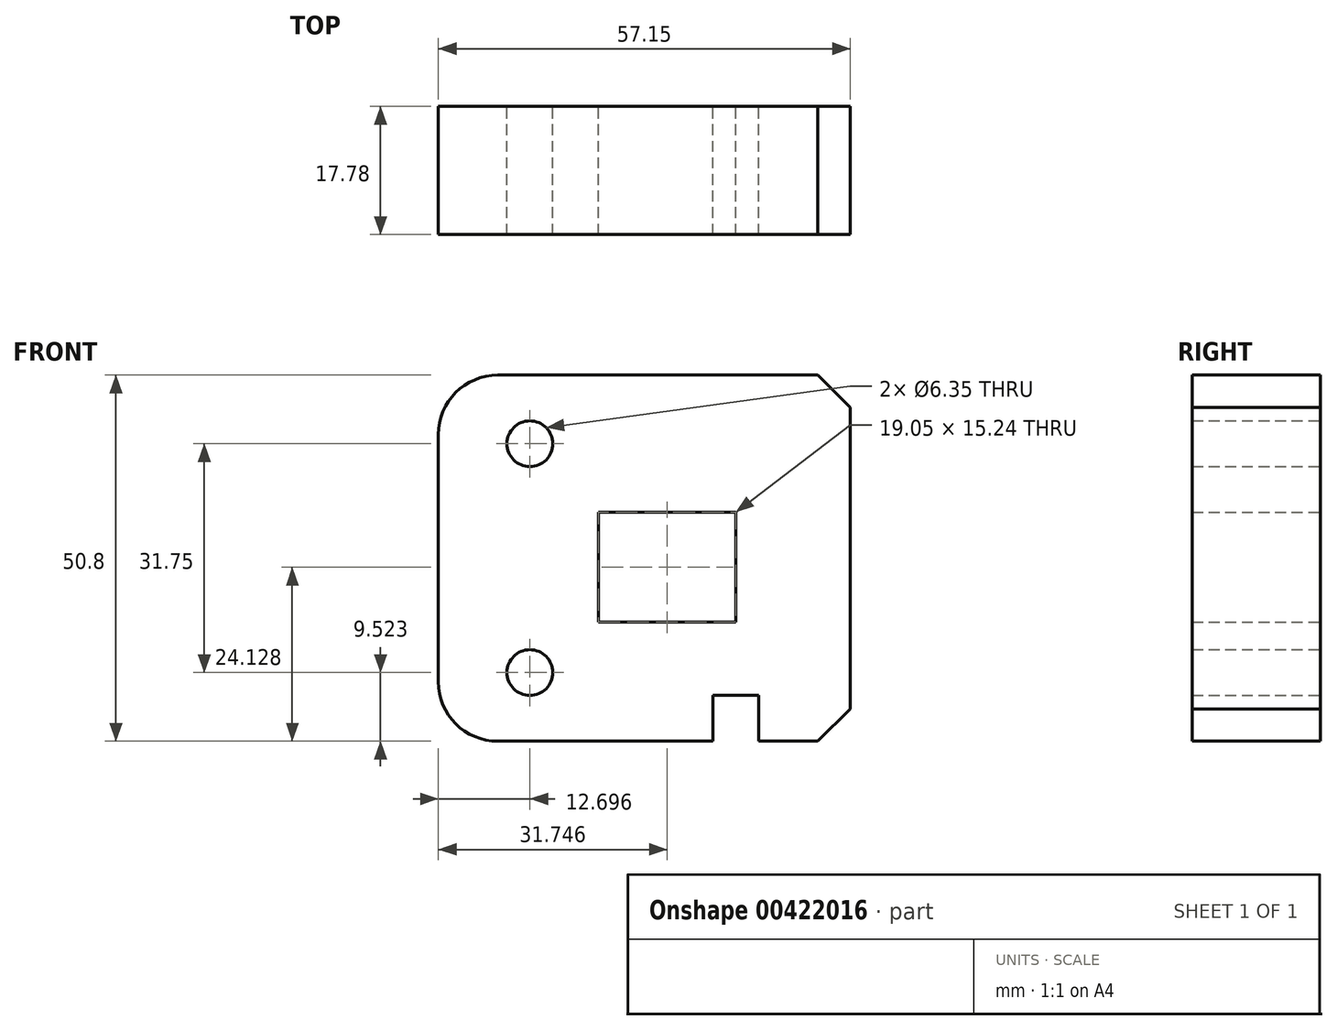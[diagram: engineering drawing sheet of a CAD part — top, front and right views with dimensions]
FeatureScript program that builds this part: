
annotation { "Feature Type Name" : "Feature", "Feature Type Description" : "" }
export const myFeature = defineFeature(function(context is Context, id is Id, definition is map)
    precondition{}
    {
        {
            var Q0;
            Q0=qCreatedBy(makeId("Front.planeOp"),FACE);
            var sketch = newSketch(context, id + "F0", { "sketchPlane" : qUnion([Q0])});
            skLineSegment(sketch, "E0.0", {"start": v(12.08, 58.2) * mm, "end": v(12.08, 26.45) * mm});
            skLineSegment(sketch, "E1.bottom", {"start": v(20.33, 16.93) * mm, "end": v(50.18, 16.93) * mm});
            skLineSegment(sketch, "E1.top", {"start": v(20.33, 67.73) * mm, "end": v(64.74, 67.73) * mm});
            skLineSegment(sketch, "E1.left", {"start": v(12.08, 25.18) * mm, "end": v(12.08, 59.47) * mm});
            skLineSegment(sketch, "E1.right", {"start": v(69.23, 21.42) * mm, "end": v(69.23, 63.24) * mm});
            skLineSegment(sketch, "E2", {"start": v(12.08, 42.33) * mm, "end": v(19.99, 42.33) * mm});
            skPoint(sketch, "E2.endSnap0", {"position": v(12.08, 42.33) * mm});
            skPoint(sketch, "E3.visualSharp", {"position": v(12.08, 67.73) * mm});
            skArc(sketch, "E3.filletArc", {"start": v(20.33, 67.73) * mm, "mid": v(14.5, 65.3) * mm, "end": v(12.08, 59.47) * mm});
            skPoint(sketch, "E4.visualSharp", {"position": v(12.08, 16.93) * mm});
            skArc(sketch, "E4.filletArc", {"start": v(12.08, 25.18) * mm, "mid": v(14.5, 19.35) * mm, "end": v(20.33, 16.93) * mm});
            skLineSegment(sketch, "E5", {"start": v(64.74, 67.73) * mm, "end": v(69.23, 63.24) * mm});
            skLineSegment(sketch, "E6", {"start": v(64.74, 16.93) * mm, "end": v(69.23, 21.42) * mm});
            skPoint(sketch, "E7.orphan", {"position": v(69.23, 67.73) * mm});
            skLineSegment(sketch, "E8", {"start": v(24.78, 16.93) * mm, "end": v(24.78, 26.45) * mm, "construction": true});
            skLineSegment(sketch, "E9", {"start": v(24.78, 67.73) * mm, "end": v(24.78, 58.2) * mm, "construction": true});
            skCircle(sketch, "E10", {"center": v(24.78, 58.2) * mm, "radius": 3.18 * mm});
            skCircle(sketch, "E11", {"center": v(24.78, 26.45) * mm, "radius": 3.18 * mm});
            skLineSegment(sketch, "E12.top", {"start": v(56.53, 23.28) * mm, "end": v(50.18, 23.28) * mm});
            skLineSegment(sketch, "E12.left", {"start": v(56.53, 16.93) * mm, "end": v(56.53, 23.28) * mm});
            skLineSegment(sketch, "E12.right", {"start": v(50.18, 16.93) * mm, "end": v(50.18, 23.28) * mm});
            skLineSegment(sketch, "E13.trimOffspring", {"start": v(56.53, 16.93) * mm, "end": v(64.74, 16.93) * mm});
            skLineSegment(sketch, "E14.bottom", {"start": v(34.3, 33.44) * mm, "end": v(53.35, 33.44) * mm});
            skLineSegment(sketch, "E14.top", {"start": v(34.3, 48.68) * mm, "end": v(53.35, 48.68) * mm});
            skLineSegment(sketch, "E14.left", {"start": v(34.3, 33.44) * mm, "end": v(34.3, 48.68) * mm});
            skLineSegment(sketch, "E14.right", {"start": v(53.35, 33.44) * mm, "end": v(53.35, 48.68) * mm});
            skSolve(sketch);
        }
        {
            var Q0;
            Q0 = qSketchRegion(id + "F0", true);
            extrude(context, id + "F1", {"entities" : qUnion([Q0]), "depth" : 17.78 * mm});
        }
    });
